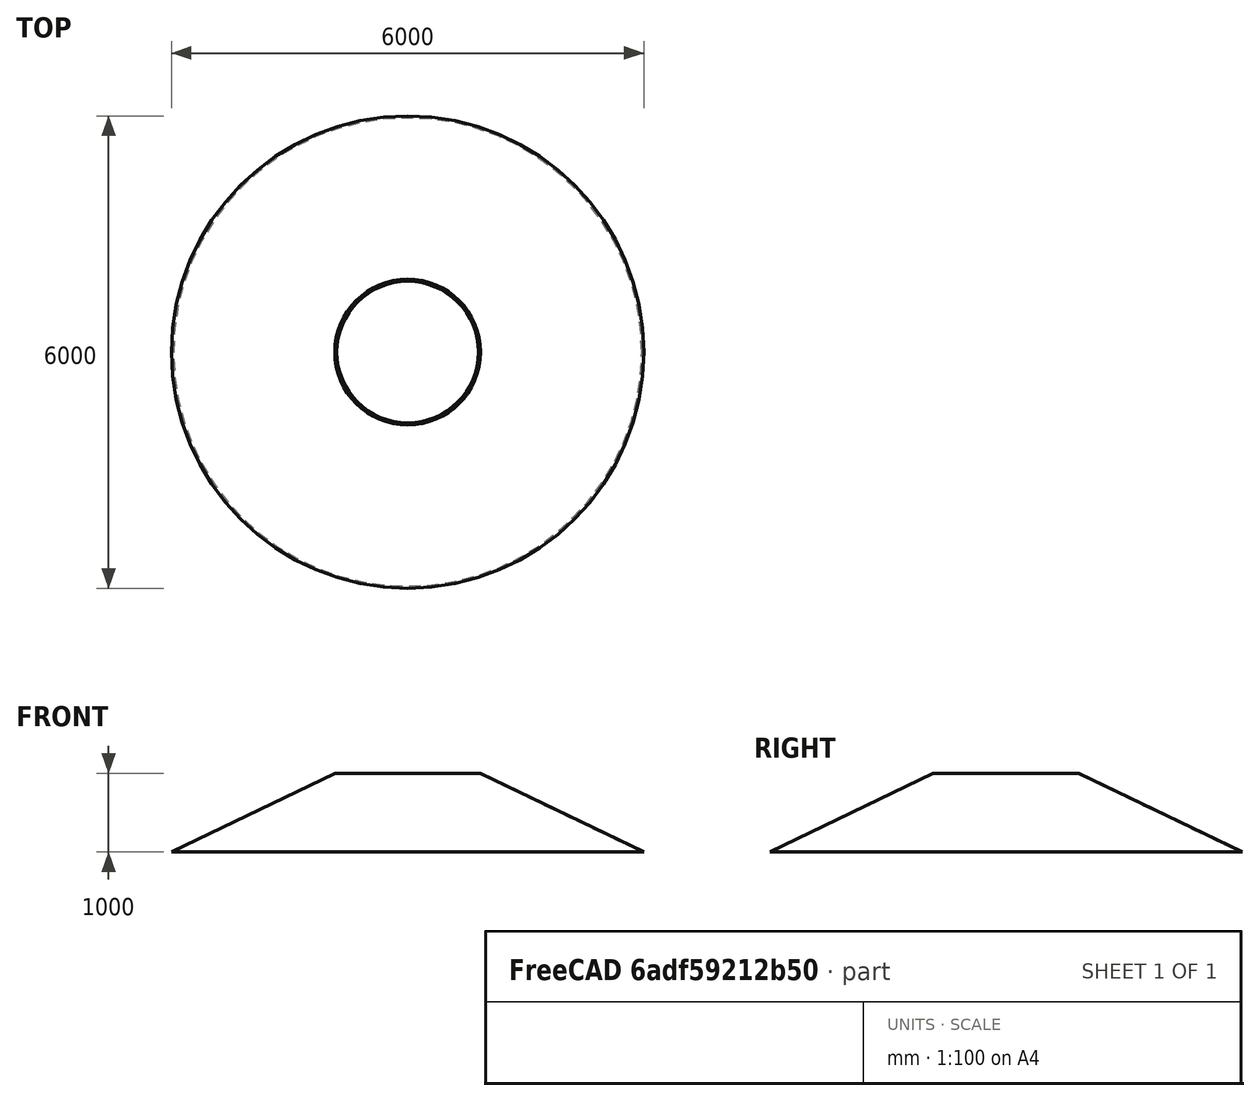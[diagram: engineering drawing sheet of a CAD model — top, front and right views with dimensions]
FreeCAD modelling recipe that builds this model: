
FCSTD DOCUMENT  (FreeCAD 0.21R33771 (Git))
Label: part3(capsule_head)
License: All rights reserved
LicenseURL: http://en.wikipedia.org/wiki/All_rights_reserved
objects: Sketcher::SketchObject×1, PartDesign::Revolution×1, PartDesign::Body×1
note: 4 computed .brp shape members not serialized (recipe doc carries the construction recipe); baked Part::Feature solids carry a one-line shape summary decoded from their .brp

FEATURE [Sketcher::SketchObject] Sketch
  FullyConstrained = true
  MapMode = 5
  Placement = pos=(0,0,0) rot=(1,0,0;1.5708rad)
  Support = -> [XZ_Plane]
  sketch-geometry (4):
    g0: LineSegment StartX=900 StartY=0 StartZ=0 EndX=2975 EndY=-1000 EndZ=0
    g1: LineSegment StartX=2975 StartY=-1000 StartZ=0 EndX=3000 EndY=-1000 EndZ=0
    g2: LineSegment StartX=3000 StartY=-1000 StartZ=0 EndX=925 EndY=0 EndZ=0
    g3: LineSegment StartX=925 StartY=0 StartZ=0 EndX=900 EndY=0 EndZ=0
  constraints (12):
    c: Coincident(g0,g1)
    c: Coincident(g1,g2)
    c: Coincident(g2,g3)
    c: Coincident(g3,g0)
    c: Horizontal(g3)
    c: Horizontal(g1)
    c: PointOnObject(g0,g-1)
    c: Equal(g3,g1)
    c: DistanceX(g3,g3) = 25
    c: DistanceX(g-1,g0) = 900
    c: DistanceX(g-1,g1) = 3000
    c: DistanceY(g0,g0) = 1000
FEATURE [PartDesign::Revolution] Revolution
  Angle = 360
  Axis = (0,2e-16,1)
  Base = (0,0,0)
  Placement = pos=(0,0,0) rot=(1,0,0;1.5708rad)
  Profile = -> Sketch
  ReferenceAxis = -> Sketch [V_Axis]
  Reversed = true
FEATURE [PartDesign::Body] Body
  Group = -> [Sketch,Revolution]
  Origin = -> Origin
  Tip = -> Revolution
